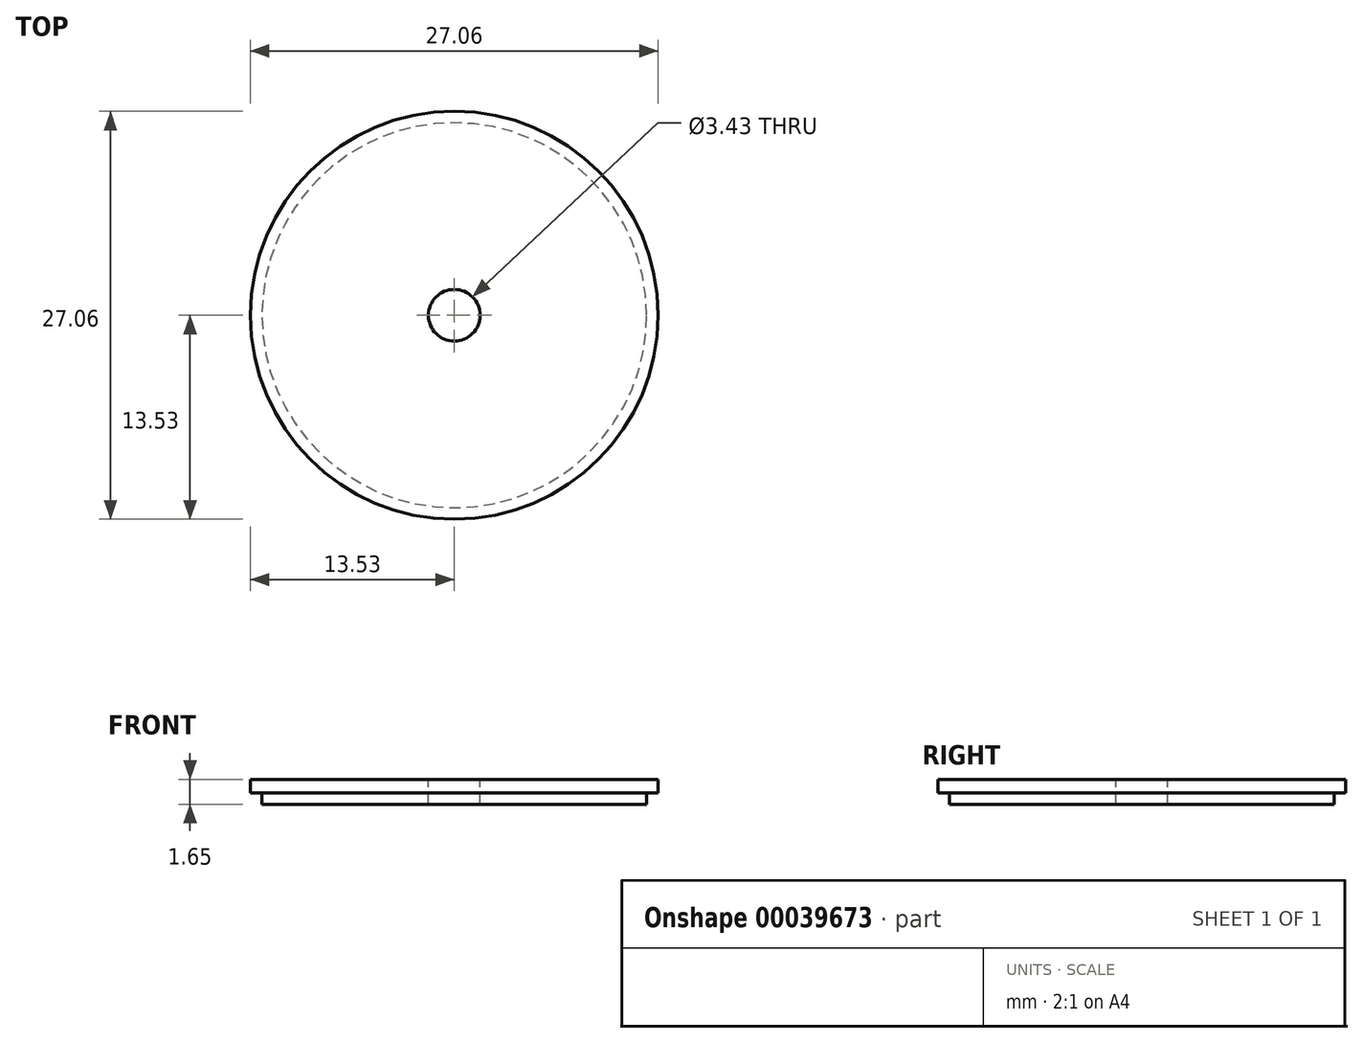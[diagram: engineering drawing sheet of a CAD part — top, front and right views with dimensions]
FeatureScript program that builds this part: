
annotation { "Feature Type Name" : "Feature", "Feature Type Description" : "" }
export const myFeature = defineFeature(function(context is Context, id is Id, definition is map)
    precondition{}
    {
        {
            var Q0;
            Q0=qCreatedBy(makeId("Top.planeOp"),FACE);
            var sketch = newSketch(context, id + "F0", { "sketchPlane" : qUnion([Q0])});
            skCircle(sketch, "E0", {"center": v(0, 0) * mm, "radius": 13.53 * mm});
            skSolve(sketch);
        }
        {
            var Q0;
            Q0 = qSketchRegion(id + "F0", true);
            extrude(context, id + "F1", {"entities" : qUnion([Q0]), "oppositeDirection" : true, "depth" : 0.89 * mm});
        }
        {
            var Q0;
            Q0=makeQuery(id+"F1.opExtrude","CAP_FACE",FACE,{"disambiguationData":[OSD([sQuery(id+"F0.wireOp",EDGE,"E0")])],"isStart":true});
            var sketch = newSketch(context, id + "F2", { "sketchPlane" : qUnion([Q0])});
            skCircle(sketch, "E1", {"center": v(0, 0) * mm, "radius": 12.76 * mm});
            skSolve(sketch);
        }
        {
            var Q0;
            Q0 = qSketchRegion(id + "F2", true);
            extrude(context, id + "F3", {"entities" : qUnion([Q0]), "operationType" : NewBodyOperationType.ADD, "oppositeDirection" : true, "depth" : 1.65 * mm});
        }
        {
            var Q0;
            Q0=makeQuery(id+"F1.opExtrude","CAP_FACE",FACE,{"disambiguationData":[OSD([sQuery(id+"F0.wireOp",EDGE,"E0")])],"isStart":true});
            var sketch = newSketch(context, id + "F4", { "sketchPlane" : qUnion([Q0])});
            skCircle(sketch, "E2", {"center": v(0, 0) * mm, "radius": 1.71 * mm});
            skSolve(sketch);
        }
        {
            var Q0;
            Q0 = qSketchRegion(id + "F4", true);
            extrude(context, id + "F5", {"entities" : qUnion([Q0]), "operationType" : NewBodyOperationType.REMOVE, "endBound" : BoundingType.THROUGH_ALL, "oppositeDirection" : true, "depth" : 25.4 * mm});
        }
    });
